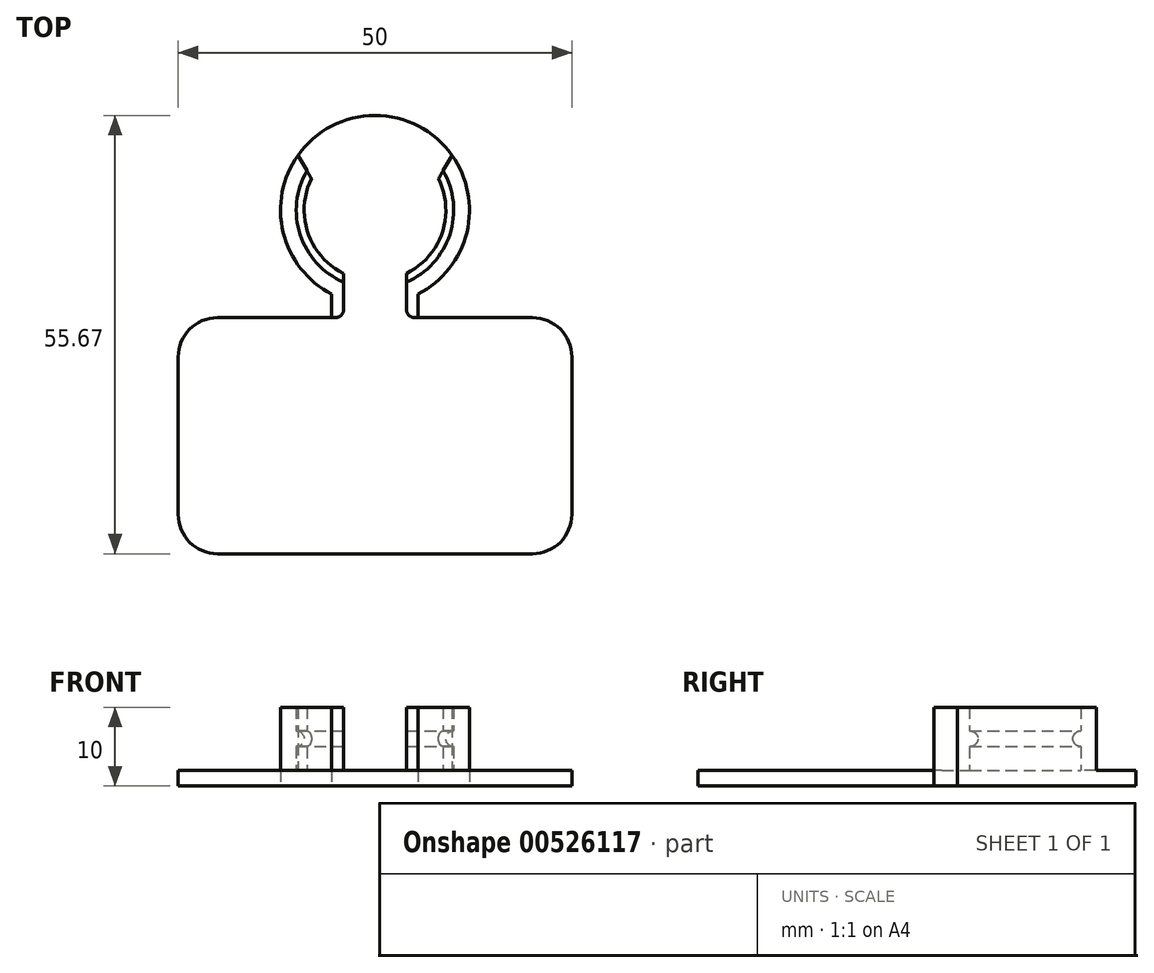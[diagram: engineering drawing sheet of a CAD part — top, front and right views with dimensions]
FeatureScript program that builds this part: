
annotation { "Feature Type Name" : "Feature", "Feature Type Description" : "" }
export const myFeature = defineFeature(function(context is Context, id is Id, definition is map)
    precondition{}
    {
        {
            var Q0;
            Q0=qCreatedBy(makeId("Top.planeOp"),FACE);
            var sketch = newSketch(context, id + "F0", { "sketchPlane" : qUnion([Q0])});
            skArc(sketch, "E0", {"start": v(-5.5, 1.5) * mm, "mid": v(0, 24.17) * mm, "end": v(5.5, 1.5) * mm});
            skArc(sketch, "E1", {"start": v(-5.5, -1.5) * mm, "mid": v(0, -24.17) * mm, "end": v(5.5, -1.5) * mm});
            skLineSegment(sketch, "E2", {"start": v(-5.5, 1.5) * mm, "end": v(-5.5, -1.5) * mm});
            skLineSegment(sketch, "E3", {"start": v(5.5, 1.5) * mm, "end": v(5.5, -1.5) * mm});
            skSolve(sketch);
        }
        {
            var Q0;
            Q0=qSketchRegion(id+"F0",true);
            extrude(context, id + "F1", {"entities" : qUnion([Q0]), "depth" : 2 * mm, "offsetDistance" : 25 * mm});
        }
        {
            var Q0;
            Q0=makeQuery(id+"F1.opExtrude","CAP_FACE",FACE,{"disambiguationData":[OSD([sQuery(id+"F0.wireOp",EDGE,"E0"),sQuery(id+"F0.wireOp",EDGE,"E1"),sQuery(id+"F0.wireOp",EDGE,"E2"),sQuery(id+"F0.wireOp",EDGE,"E3")])],"isStart":false});
            var sketch = newSketch(context, id + "F2", { "sketchPlane" : qUnion([Q0])});
            skArc(sketch, "E4", {"start": v(8.66, 17.17) * mm, "mid": v(9.5, 9.04) * mm, "end": v(4, 3) * mm});
            skArc(sketch, "E5", {"start": v(9.78, 19.11) * mm, "mid": v(11.66, 9.33) * mm, "end": v(5.5, 1.5) * mm});
            skArc(sketch, "E6", {"start": v(-8.66, 17.17) * mm, "mid": v(-9.5, 9.04) * mm, "end": v(-4, 3) * mm});
            skArc(sketch, "E7", {"start": v(5.5, -3.81) * mm, "mid": v(9.59, -9.32) * mm, "end": v(9.17, -16.17) * mm});
            skLineSegment(sketch, "E8", {"start": v(9.78, 19.11) * mm, "end": v(8.66, 17.17) * mm});
            skLineSegment(sketch, "E9", {"start": v(-8.66, 17.17) * mm, "end": v(-9.78, 19.11) * mm});
            skLineSegment(sketch, "E10", {"start": v(5.5, 1.5) * mm, "end": v(5.5, -3.81) * mm});
            skLineSegment(sketch, "E11", {"start": v(-4, 3) * mm, "end": v(-4, -6.24) * mm});
            skLineSegment(sketch, "E12", {"start": v(-4, -6.24) * mm, "end": v(-9.17, -16.17) * mm});
            skLineSegment(sketch, "E13", {"start": v(9.17, -16.17) * mm, "end": v(4, -6.24) * mm});
            skLineSegment(sketch, "E14", {"start": v(4, -6.24) * mm, "end": v(4, 3) * mm});
            skArc(sketch, "E15", {"start": v(-9.78, 19.11) * mm, "mid": v(-11.66, 9.33) * mm, "end": v(-5.5, 1.5) * mm});
            skArc(sketch, "E16", {"start": v(-9.17, -16.17) * mm, "mid": v(-9.59, -9.32) * mm, "end": v(-5.5, -3.81) * mm});
            skLineSegment(sketch, "E17", {"start": v(-5.5, 1.5) * mm, "end": v(-5.5, -3.81) * mm});
            skArc(sketch, "E18.0", {"start": v(-5.5, 1.5) * mm, "mid": v(0, 24.17) * mm, "end": v(5.5, 1.5) * mm, "construction": true});
            skArc(sketch, "E19.0", {"start": v(-5.5, -1.5) * mm, "mid": v(0, -24.17) * mm, "end": v(5.5, -1.5) * mm, "construction": true});
            skSolve(sketch);
        }
        {
            var Q0;
            Q0=qSketchRegion(id+"F2",true);
            extrude(context, id + "F3", {"entities" : qUnion([Q0]), "operationType" : NewBodyOperationType.ADD, "depth" : 3 * mm, "offsetDistance" : 25 * mm});
        }
        {
            var Q0;
            Q0=makeQuery(id+"F3.opExtrude","CAP_FACE",FACE,{"disambiguationData":[OSD([sQuery(id+"F2.wireOp",EDGE,"E4"),sQuery(id+"F2.wireOp",EDGE,"E5"),sQuery(id+"F2.wireOp",EDGE,"E7"),sQuery(id+"F2.wireOp",EDGE,"E8"),sQuery(id+"F2.wireOp",EDGE,"E10"),sQuery(id+"F2.wireOp",EDGE,"E13"),sQuery(id+"F2.wireOp",EDGE,"E14")])],"isStart":false});
            var sketch = newSketch(context, id + "F4", { "sketchPlane" : qUnion([Q0])});
            skArc(sketch, "E20", {"start": v(-9.78, 19.11) * mm, "mid": v(-11.66, 9.33) * mm, "end": v(-5.5, 1.5) * mm});
            skArc(sketch, "E21", {"start": v(9.78, 19.11) * mm, "mid": v(11.66, 9.33) * mm, "end": v(5.5, 1.5) * mm});
            skArc(sketch, "E22", {"start": v(8.07, 16.15) * mm, "mid": v(8.53, 9.28) * mm, "end": v(4, 4.1) * mm});
            skArc(sketch, "E23", {"start": v(-8.07, 16.15) * mm, "mid": v(-8.53, 9.28) * mm, "end": v(-4, 4.1) * mm});
            skArc(sketch, "E24", {"start": v(5.5, -5.04) * mm, "mid": v(8.6, -9.53) * mm, "end": v(8.55, -14.98) * mm});
            skArc(sketch, "E25", {"start": v(-5.5, -5.04) * mm, "mid": v(-8.6, -9.53) * mm, "end": v(-8.55, -14.98) * mm});
            skLineSegment(sketch, "E26", {"start": v(-5.5, 1.5) * mm, "end": v(-5.5, -5.04) * mm});
            skLineSegment(sketch, "E27", {"start": v(5.5, 1.5) * mm, "end": v(5.5, -5.04) * mm});
            skLineSegment(sketch, "E28", {"start": v(-4, 4.1) * mm, "end": v(-4, -6.24) * mm});
            skLineSegment(sketch, "E29", {"start": v(-4, -6.24) * mm, "end": v(-8.55, -14.98) * mm});
            skLineSegment(sketch, "E30", {"start": v(4, 4.1) * mm, "end": v(4, -6.24) * mm});
            skLineSegment(sketch, "E31", {"start": v(4, -6.24) * mm, "end": v(8.55, -14.98) * mm});
            skLineSegment(sketch, "E32", {"start": v(8.07, 16.15) * mm, "end": v(9.78, 19.11) * mm});
            skLineSegment(sketch, "E33", {"start": v(-9.78, 19.11) * mm, "end": v(-8.07, 16.15) * mm});
            skLineSegment(sketch, "E34.0", {"start": v(-8.66, 17.17) * mm, "end": v(-9.78, 19.11) * mm, "construction": true});
            skLineSegment(sketch, "E35.0", {"start": v(9.78, 19.11) * mm, "end": v(8.66, 17.17) * mm, "construction": true});
            skLineSegment(sketch, "E36.0", {"start": v(-4, -6.24) * mm, "end": v(-9.17, -16.17) * mm, "construction": true});
            skLineSegment(sketch, "E37.0", {"start": v(9.17, -16.17) * mm, "end": v(4, -6.24) * mm, "construction": true});
            skArc(sketch, "E38.0", {"start": v(-9.78, 19.11) * mm, "mid": v(0, 24.17) * mm, "end": v(9.78, 19.11) * mm, "construction": true});
            skArc(sketch, "E39.0", {"start": v(-5.5, -1.5) * mm, "mid": v(0, -24.17) * mm, "end": v(5.5, -1.5) * mm, "construction": true});
            skSolve(sketch);
        }
        {
            var Q0;
            Q0=qSketchRegion(id+"F4",true);
            extrude(context, id + "F5", {"entities" : qUnion([Q0]), "operationType" : NewBodyOperationType.ADD, "depth" : 2 * mm, "offsetDistance" : 25 * mm});
        }
        {
            var Q0;
            Q0=makeQuery(id+"F5.opExtrude","CAP_FACE",FACE,{"disambiguationData":[OSD([sQuery(id+"F4.wireOp",EDGE,"E21"),sQuery(id+"F4.wireOp",EDGE,"E22"),sQuery(id+"F4.wireOp",EDGE,"E24"),sQuery(id+"F4.wireOp",EDGE,"E27"),sQuery(id+"F4.wireOp",EDGE,"E30"),sQuery(id+"F4.wireOp",EDGE,"E31"),sQuery(id+"F4.wireOp",EDGE,"E32")])],"isStart":false});
            var sketch = newSketch(context, id + "F6", { "sketchPlane" : qUnion([Q0])});
            skArc(sketch, "E40", {"start": v(8.66, 17.17) * mm, "mid": v(9.5, 9.04) * mm, "end": v(4, 3) * mm});
            skArc(sketch, "E41", {"start": v(9.78, 19.11) * mm, "mid": v(11.66, 9.33) * mm, "end": v(5.5, 1.5) * mm});
            skArc(sketch, "E42", {"start": v(-8.66, 17.17) * mm, "mid": v(-9.5, 9.04) * mm, "end": v(-4, 3) * mm});
            skArc(sketch, "E43", {"start": v(5.5, -3.81) * mm, "mid": v(9.59, -9.32) * mm, "end": v(9.17, -16.17) * mm});
            skLineSegment(sketch, "E44", {"start": v(9.78, 19.11) * mm, "end": v(8.66, 17.17) * mm});
            skLineSegment(sketch, "E45", {"start": v(-8.66, 17.17) * mm, "end": v(-9.78, 19.11) * mm});
            skLineSegment(sketch, "E46", {"start": v(5.5, 1.5) * mm, "end": v(5.5, -3.81) * mm});
            skLineSegment(sketch, "E47", {"start": v(-4, 3) * mm, "end": v(-4, -6.24) * mm});
            skLineSegment(sketch, "E48", {"start": v(-4, -6.24) * mm, "end": v(-9.17, -16.17) * mm});
            skLineSegment(sketch, "E49", {"start": v(9.17, -16.17) * mm, "end": v(4, -6.24) * mm});
            skLineSegment(sketch, "E50", {"start": v(4, -6.24) * mm, "end": v(4, 3) * mm});
            skArc(sketch, "E51", {"start": v(-9.78, 19.11) * mm, "mid": v(-11.66, 9.33) * mm, "end": v(-5.5, 1.5) * mm});
            skArc(sketch, "E52", {"start": v(-9.17, -16.17) * mm, "mid": v(-9.59, -9.32) * mm, "end": v(-5.5, -3.81) * mm});
            skLineSegment(sketch, "E53", {"start": v(-5.5, 1.5) * mm, "end": v(-5.5, -3.81) * mm});
            skArc(sketch, "E54.0", {"start": v(-5.5, -1.5) * mm, "mid": v(0, -24.17) * mm, "end": v(5.5, -1.5) * mm, "construction": true});
            skArc(sketch, "E55.0", {"start": v(-9.78, 19.11) * mm, "mid": v(0, 24.17) * mm, "end": v(9.78, 19.11) * mm, "construction": true});
            skSolve(sketch);
        }
        {
            var Q0;
            Q0=qSketchRegion(id+"F6",true);
            extrude(context, id + "F7", {"entities" : qUnion([Q0]), "operationType" : NewBodyOperationType.ADD, "depth" : 3 * mm, "offsetDistance" : 25 * mm});
        }
        {
            var Q0;
            Q0=makeQuery(id+"F5.opExtrude","CAP_EDGE",EDGE,{"disambiguationData":[OSD([sQuery(id+"F4.wireOp",EDGE,"E22")])],"isStart":false});
            var Q1;
            Q1=makeQuery(id+"F5.opExtrude","CAP_EDGE",EDGE,{"disambiguationData":[OSD([sQuery(id+"F4.wireOp",EDGE,"E23")])],"isStart":false});
            var Q2;
            Q2=makeQuery(id+"F5.opExtrude","CAP_EDGE",EDGE,{"disambiguationData":[OSD([sQuery(id+"F4.wireOp",EDGE,"E23")])],"isStart":true});
            var Q3;
            Q3=makeQuery(id+"F5.opExtrude","CAP_EDGE",EDGE,{"disambiguationData":[OSD([sQuery(id+"F4.wireOp",EDGE,"E22")])],"isStart":true});
            var Q4;
            Q4=makeQuery(id+"F5.opExtrude","CAP_EDGE",EDGE,{"disambiguationData":[OSD([sQuery(id+"F4.wireOp",EDGE,"E25")])],"isStart":true});
            var Q5;
            Q5=makeQuery(id+"F5.opExtrude","CAP_EDGE",EDGE,{"disambiguationData":[OSD([sQuery(id+"F4.wireOp",EDGE,"E25")])],"isStart":false});
            var Q6;
            Q6=makeQuery(id+"F5.opExtrude","CAP_EDGE",EDGE,{"disambiguationData":[OSD([sQuery(id+"F4.wireOp",EDGE,"E24")])],"isStart":false});
            var Q7;
            Q7=makeQuery(id+"F5.opExtrude","CAP_EDGE",EDGE,{"disambiguationData":[OSD([sQuery(id+"F4.wireOp",EDGE,"E24")])],"isStart":true});
            fillet(context, id + "F8", {"entities" : qUnion([Q0, Q1, Q2, Q3, Q4, Q5, Q6, Q7]), "radius" : 1 * mm, "tangentPropagation" : true, "allowEdgeOverflow" : false});
        }
        {
            var Q0;
            Q0=makeQuery(id+"F7.opExtrude","CAP_FACE",FACE,{"disambiguationData":[OSD([sQuery(id+"F6.wireOp",EDGE,"E40"),sQuery(id+"F6.wireOp",EDGE,"E41"),sQuery(id+"F6.wireOp",EDGE,"E43"),sQuery(id+"F6.wireOp",EDGE,"E44"),sQuery(id+"F6.wireOp",EDGE,"E46"),sQuery(id+"F6.wireOp",EDGE,"E49"),sQuery(id+"F6.wireOp",EDGE,"E50")])],"isStart":false});
            var sketch = newSketch(context, id + "F9", { "sketchPlane" : qUnion([Q0])});
            skLineSegment(sketch, "E56.bottom", {"start": v(-10, -1.5) * mm, "end": v(10, -1.5) * mm});
            skLineSegment(sketch, "E56.top", {"start": v(-10, -16.17) * mm, "end": v(10, -16.17) * mm});
            skLineSegment(sketch, "E56.left", {"start": v(-10, -1.5) * mm, "end": v(-10, -16.17) * mm});
            skLineSegment(sketch, "E56.right", {"start": v(10, -1.5) * mm, "end": v(10, -16.17) * mm});
            skSolve(sketch);
        }
        {
            var Q0;
            Q0=qSketchRegion(id+"F9",true);
            extrude(context, id + "F10", {"entities" : qUnion([Q0]), "operationType" : NewBodyOperationType.REMOVE, "oppositeDirection" : true, "depth" : 8 * mm, "offsetDistance" : 25 * mm});
        }
        {
            var Q0;
            Q0=makeQuery(id+"F10.boolean.opBoolean","MERGE",FACE,{"derivedFrom":[makeQuery(id+"F1.opExtrude","CAP_FACE",FACE,{"disambiguationData":[OSD([sQuery(id+"F0.wireOp",EDGE,"E0"),sQuery(id+"F0.wireOp",EDGE,"E1"),sQuery(id+"F0.wireOp",EDGE,"E2"),sQuery(id+"F0.wireOp",EDGE,"E3")])],"isStart":false}),makeQuery(id+"F10.opExtrude","CAP_FACE",FACE,{"disambiguationData":[OSD([sQuery(id+"F9.wireOp",EDGE,"E56.bottom"),sQuery(id+"F9.wireOp",EDGE,"E56.top"),sQuery(id+"F9.wireOp",EDGE,"E56.left"),sQuery(id+"F9.wireOp",EDGE,"E56.right")])],"isStart":false})]});
            var sketch = newSketch(context, id + "F11", { "sketchPlane" : qUnion([Q0])});
            skLineSegment(sketch, "E57.bottom", {"start": v(-25, -1.5) * mm, "end": v(25, -1.5) * mm});
            skLineSegment(sketch, "E57.top", {"start": v(-25, -31.5) * mm, "end": v(25, -31.5) * mm});
            skLineSegment(sketch, "E57.left", {"start": v(-25, -1.5) * mm, "end": v(-25, -31.5) * mm});
            skLineSegment(sketch, "E57.right", {"start": v(25, -1.5) * mm, "end": v(25, -31.5) * mm});
            skSolve(sketch);
        }
        {
            var Q0;
            Q0=qSketchRegion(id+"F11",true);
            extrude(context, id + "F12", {"entities" : qUnion([Q0]), "operationType" : NewBodyOperationType.ADD, "oppositeDirection" : true, "depth" : 2 * mm, "offsetDistance" : 25 * mm});
        }
        {
            var Q0;
            Q0=makeQuery(id+"F10.boolean.opBoolean","INTERSECT",EDGE,{"derivedFrom":[makeQuery(id+"F7.boolean.opBoolean","MERGE",FACE,{"derivedFrom":[makeQuery(id+"F5.boolean.opBoolean","MERGE",FACE,{"derivedFrom":[makeQuery(id+"F3.opExtrude","SWEPT_FACE",FACE,{"disambiguationData":[OSD([sQuery(id+"F2.wireOp",EDGE,"E11")])]}),makeQuery(id+"F5.opExtrude","SWEPT_FACE",FACE,{"disambiguationData":[OSD([sQuery(id+"F4.wireOp",EDGE,"E28")])]})]}),makeQuery(id+"F7.opExtrude","SWEPT_FACE",FACE,{"disambiguationData":[OSD([sQuery(id+"F6.wireOp",EDGE,"E47")])]})]}),makeQuery(id+"F10.opExtrude","SWEPT_FACE",FACE,{"disambiguationData":[OSD([sQuery(id+"F9.wireOp",EDGE,"E56.bottom")])]})]});
            var Q1;
            Q1=makeQuery(id+"F10.boolean.opBoolean","INTERSECT",EDGE,{"derivedFrom":[makeQuery(id+"F7.boolean.opBoolean","MERGE",FACE,{"derivedFrom":[makeQuery(id+"F5.boolean.opBoolean","MERGE",FACE,{"derivedFrom":[makeQuery(id+"F3.opExtrude","SWEPT_FACE",FACE,{"disambiguationData":[OSD([sQuery(id+"F2.wireOp",EDGE,"E14")])]}),makeQuery(id+"F5.opExtrude","SWEPT_FACE",FACE,{"disambiguationData":[OSD([sQuery(id+"F4.wireOp",EDGE,"E30")])]})]}),makeQuery(id+"F7.opExtrude","SWEPT_FACE",FACE,{"disambiguationData":[OSD([sQuery(id+"F6.wireOp",EDGE,"E50")])]})]}),makeQuery(id+"F10.opExtrude","SWEPT_FACE",FACE,{"disambiguationData":[OSD([sQuery(id+"F9.wireOp",EDGE,"E56.bottom")])]})]});
            fillet(context, id + "F13", {"entities" : qUnion([Q0, Q1]), "radius" : 1 * mm, "tangentPropagation" : true, "allowEdgeOverflow" : false});
        }
        {
            var Q0;
            Q0=makeQuery(id+"F12.opExtrude","SWEPT_EDGE",EDGE,{"disambiguationData":[OSD([sQuery(id+"F11.wireOp",EDGE,"E57.bottom"),sQuery(id+"F11.wireOp",EDGE,"E57.left")])]});
            var Q1;
            Q1=makeQuery(id+"F12.opExtrude","SWEPT_EDGE",EDGE,{"disambiguationData":[OSD([sQuery(id+"F11.wireOp",EDGE,"E57.top"),sQuery(id+"F11.wireOp",EDGE,"E57.left")])]});
            var Q2;
            Q2=makeQuery(id+"F12.opExtrude","SWEPT_EDGE",EDGE,{"disambiguationData":[OSD([sQuery(id+"F11.wireOp",EDGE,"E57.top"),sQuery(id+"F11.wireOp",EDGE,"E57.right")])]});
            var Q3;
            Q3=makeQuery(id+"F12.opExtrude","SWEPT_EDGE",EDGE,{"disambiguationData":[OSD([sQuery(id+"F11.wireOp",EDGE,"E57.bottom"),sQuery(id+"F11.wireOp",EDGE,"E57.right")])]});
            fillet(context, id + "F14", {"entities" : qUnion([Q0, Q1, Q2, Q3]), "radius" : 5 * mm, "tangentPropagation" : true, "allowEdgeOverflow" : false});
        }
    });
